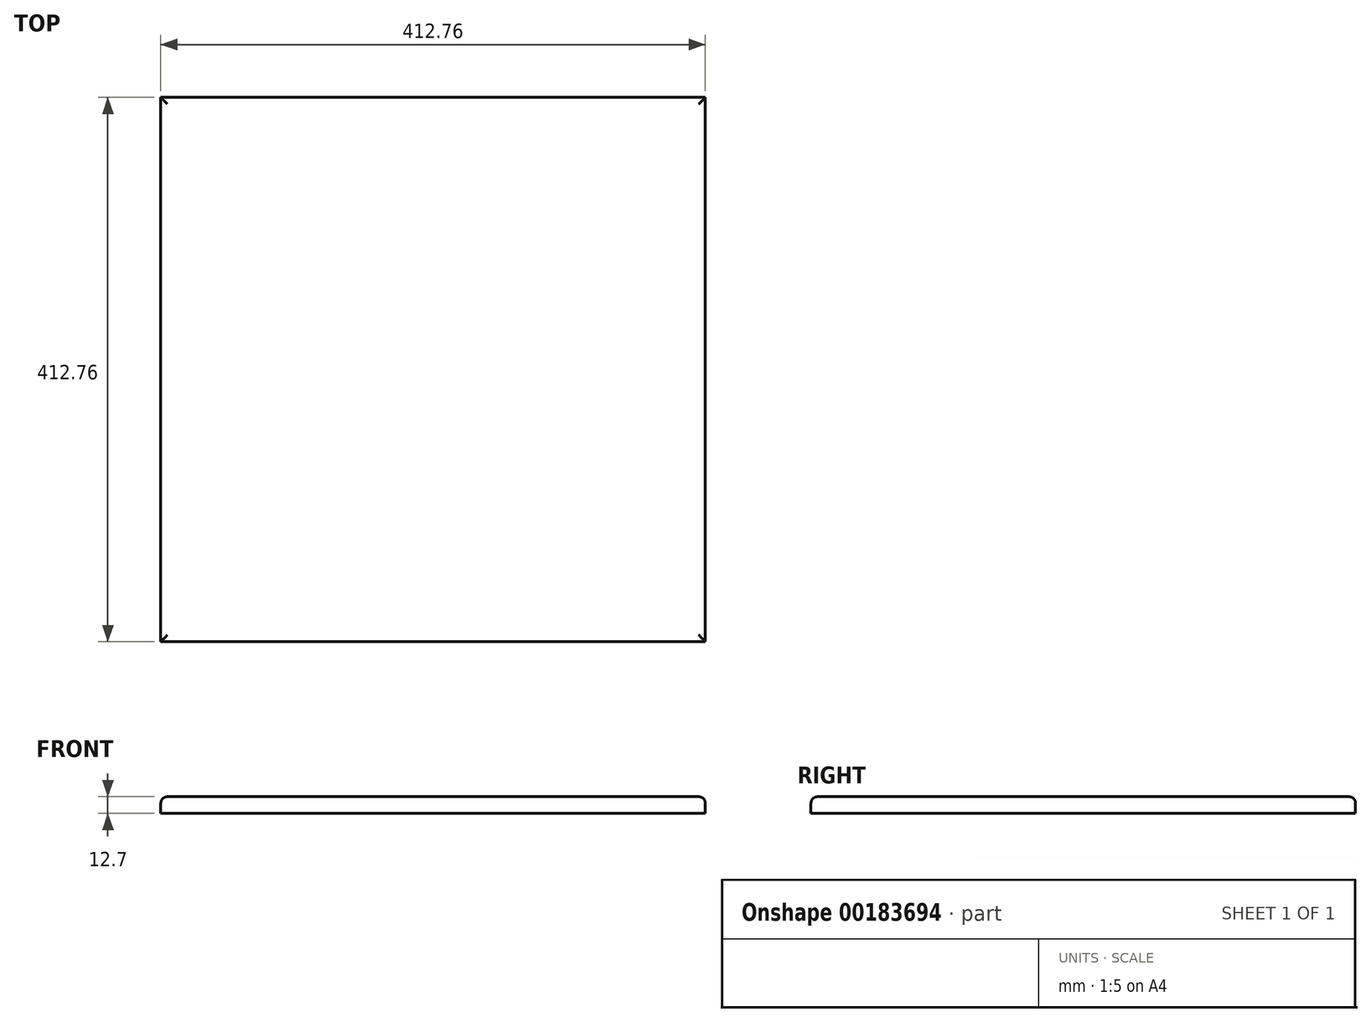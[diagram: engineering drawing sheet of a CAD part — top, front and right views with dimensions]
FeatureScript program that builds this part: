
annotation { "Feature Type Name" : "Feature", "Feature Type Description" : "" }
export const myFeature = defineFeature(function(context is Context, id is Id, definition is map)
    precondition{}
    {
        {
            var Q0;
            Q0=qCreatedBy(makeId("Front.planeOp"),FACE);
            var sketch = newSketch(context, id + "F0", { "sketchPlane" : qUnion([Q0])});
            skLineSegment(sketch, "E0.bottom", {"start": v(206.38, 6.35) * mm, "end": v(-206.38, 6.35) * mm});
            skLineSegment(sketch, "E0.top", {"start": v(206.38, -6.35) * mm, "end": v(-206.38, -6.35) * mm});
            skLineSegment(sketch, "E0.left", {"start": v(206.38, 6.35) * mm, "end": v(206.38, -6.35) * mm});
            skLineSegment(sketch, "E0.right", {"start": v(-206.38, 6.35) * mm, "end": v(-206.38, -6.35) * mm});
            skPoint(sketch, "E0.middle", {"position": v(0, 0) * mm});
            skSolve(sketch);
        }
        {
            var Q0;
            Q0 = qSketchRegion(id + "F0", true);
            extrude(context, id + "F1", {"entities" : qUnion([Q0]), "endBound" : BoundingType.SYMMETRIC, "depth" : 412.75 * mm});
        }
        {
            var Q0;
            Q0=makeQuery(id+"F1.opExtrude","SWEPT_EDGE",EDGE,{"disambiguationData":[OSD([sQuery(id+"F0.wireOp",EDGE,"E0.bottom"),sQuery(id+"F0.wireOp",EDGE,"E0.right")])]});
            var Q1;
            Q1=makeQuery(id+"F1.opExtrude","CAP_EDGE",EDGE,{"disambiguationData":[OSD([sQuery(id+"F0.wireOp",EDGE,"E0.bottom")])],"isStart":false});
            var Q2;
            Q2=makeQuery(id+"F1.opExtrude","SWEPT_EDGE",EDGE,{"disambiguationData":[OSD([sQuery(id+"F0.wireOp",EDGE,"E0.bottom"),sQuery(id+"F0.wireOp",EDGE,"E0.left")])]});
            var Q3;
            Q3=makeQuery(id+"F1.opExtrude","CAP_EDGE",EDGE,{"disambiguationData":[OSD([sQuery(id+"F0.wireOp",EDGE,"E0.bottom")])],"isStart":true});
            fillet(context, id + "F2", {"entities" : qUnion([Q0, Q1, Q2, Q3]), "radius" : 5.08 * mm, "tangentPropagation" : true, "allowEdgeOverflow" : false});
        }
    });
